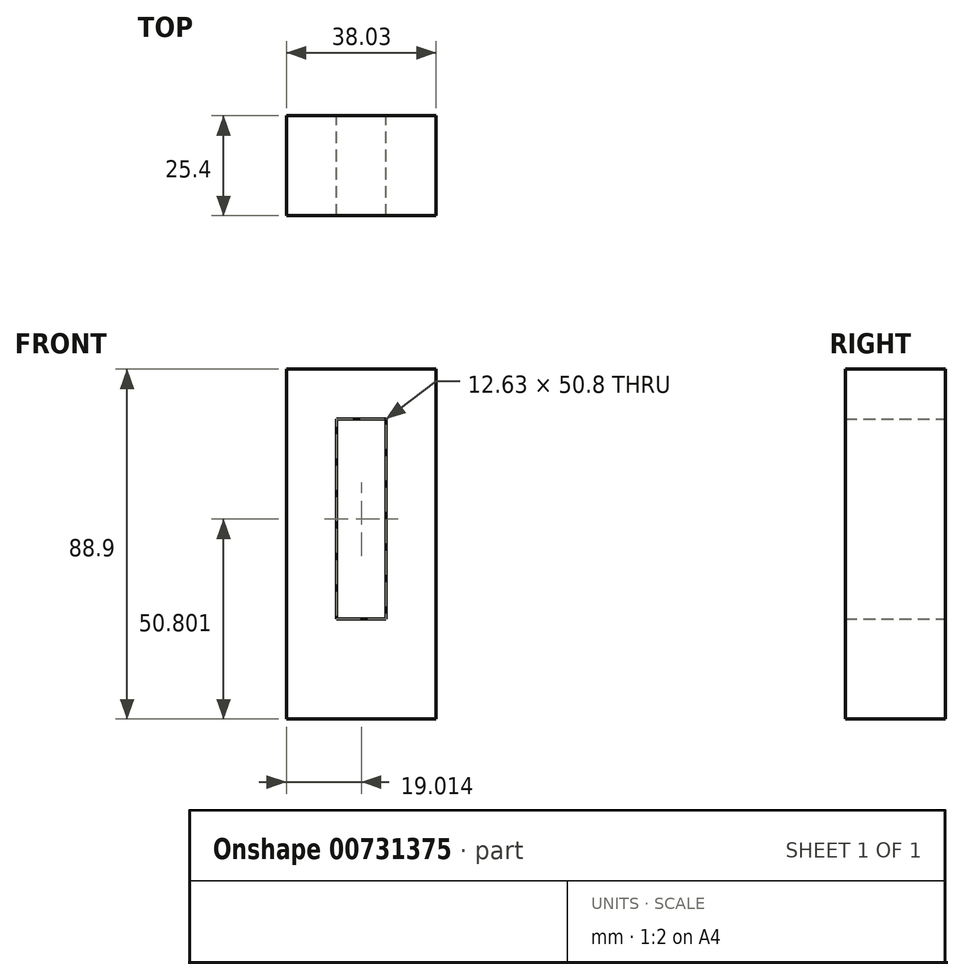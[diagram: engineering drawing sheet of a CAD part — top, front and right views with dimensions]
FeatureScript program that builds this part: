
annotation { "Feature Type Name" : "Feature", "Feature Type Description" : "" }
export const myFeature = defineFeature(function(context is Context, id is Id, definition is map)
    precondition{}
    {
        {
            var Q0;
            Q0=qCreatedBy(makeId("Front.planeOp"),FACE);
            var sketch = newSketch(context, id + "F0", { "sketchPlane" : qUnion([Q0])});
            skLineSegment(sketch, "E0.bottom", {"start": v(-20.56, 64) * mm, "end": v(30.24, 64) * mm});
            skLineSegment(sketch, "E0.top", {"start": v(-20.56, -88.4) * mm, "end": v(30.24, -88.4) * mm});
            skLineSegment(sketch, "E0.left", {"start": v(-20.56, 64) * mm, "end": v(-20.56, -88.4) * mm});
            skLineSegment(sketch, "E0.right", {"start": v(30.24, 64) * mm, "end": v(30.24, -88.4) * mm});
            skLineSegment(sketch, "E1.bottom", {"start": v(-80.3, -54.14) * mm, "end": v(-67.6, -54.14) * mm});
            skLineSegment(sketch, "E1.top", {"start": v(-80.3, -3.34) * mm, "end": v(-67.6, -3.34) * mm});
            skLineSegment(sketch, "E1.left", {"start": v(-80.3, -54.14) * mm, "end": v(-80.3, -3.34) * mm});
            skLineSegment(sketch, "E1.right", {"start": v(-67.6, -54.14) * mm, "end": v(-67.6, -3.34) * mm});
            skLineSegment(sketch, "E2.bottom", {"start": v(-67.6, -54.14) * mm, "end": v(-54.97, -54.14) * mm});
            skLineSegment(sketch, "E2.top", {"start": v(-67.6, -3.34) * mm, "end": v(-54.9, -3.34) * mm});
            skLineSegment(sketch, "E3.bottom", {"start": v(-54.97, -54.14) * mm, "end": v(-42.27, -54.14) * mm});
            skLineSegment(sketch, "E3.top", {"start": v(-54.97, -3.34) * mm, "end": v(-42.27, -3.34) * mm});
            skLineSegment(sketch, "E3.left", {"start": v(-54.97, -54.14) * mm, "end": v(-54.97, -3.34) * mm});
            skLineSegment(sketch, "E3.right", {"start": v(-42.27, -54.14) * mm, "end": v(-42.27, -3.34) * mm});
            skLineSegment(sketch, "E4.bottom", {"start": v(-80.3, -3.34) * mm, "end": v(-42.27, -3.34) * mm});
            skLineSegment(sketch, "E4.top", {"start": v(-80.3, 9.36) * mm, "end": v(-42.27, 9.36) * mm});
            skLineSegment(sketch, "E4.left", {"start": v(-80.3, -3.34) * mm, "end": v(-80.3, 9.36) * mm});
            skLineSegment(sketch, "E4.right", {"start": v(-42.27, -3.34) * mm, "end": v(-42.27, 9.36) * mm});
            skLineSegment(sketch, "E5.bottom", {"start": v(-80.3, -54.14) * mm, "end": v(-42.27, -54.14) * mm});
            skLineSegment(sketch, "E5.top", {"start": v(-80.3, -79.54) * mm, "end": v(-42.27, -79.54) * mm});
            skLineSegment(sketch, "E5.left", {"start": v(-80.3, -54.14) * mm, "end": v(-80.3, -79.54) * mm});
            skLineSegment(sketch, "E5.right", {"start": v(-42.27, -54.14) * mm, "end": v(-42.27, -79.54) * mm});
            skLineSegment(sketch, "E6.bottom", {"start": v(-67.6, 9.36) * mm, "end": v(-54.9, 9.36) * mm});
            skSolve(sketch);
        }
        {
            var Q0;
            Q0=makeQuery(id+"F0.imprint","IMPRINT",FACE,{"disambiguationData":[TD([[makeQuery(id+"F0.imprint","IMPRINT",EDGE,{"derivedFrom":sQuery(id+"F0.wireOp",EDGE,"E4.top")}),-1.0]])]});
            var Q1;
            {var subQ0=sQuery(id+"F0.wireOp",EDGE,"E1.left");Q1=makeQuery(id+"F0.imprint","IMPRINT",FACE,{"disambiguationData":[TD([[makeQuery(id+"F0.imprint","IMPRINT",EDGE,{"derivedFrom":subQ0}),-1.0]])]});}
            var Q2;
            {var subQ1=sQuery(id+"F0.wireOp",EDGE,"E3.left");Q2=makeQuery(id+"F0.imprint","IMPRINT",FACE,{"disambiguationData":[TD([[makeQuery(id+"F0.imprint","IMPRINT",EDGE,{"derivedFrom":subQ1}),-1.0]])]});}
            var Q3;
            Q3=makeQuery(id+"F0.imprint","IMPRINT",FACE,{"disambiguationData":[TD([[makeQuery(id+"F0.imprint","IMPRINT",EDGE,{"derivedFrom":sQuery(id+"F0.wireOp",EDGE,"E5.top")}),1.0]])]});
            extrude(context, id + "F1", {"entities" : qUnion([Q0, Q1, Q2, Q3]), "depth" : 25.4 * mm, "offsetDistance" : 25.4 * mm});
        }
    });
